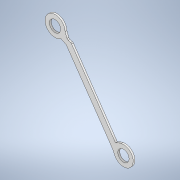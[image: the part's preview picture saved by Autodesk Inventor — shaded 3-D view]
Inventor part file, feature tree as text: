
AUTODESK INVENTOR PART (.ipt)
format: ipt  version: 2022 (Build 260153000, 153)  size: 147,968 bytes
history: native  units: in
note: dims shown in document units (in); Inventor stores cm internally (conversion verified against a paired STEP export)
features: other x1, extrude x1, sketch x1
ambient origin geometry x8: Origin, YZ Plane, XZ Plane, XY Plane, X Axis, Y Axis, Z Axis, Center Point
bodies: Body1 (feature_tree)
feature tree (3):
  other  "Sólido1"
  extrude  "Extrusión1"  Depth=0.0787in
  sketch  "Boceto1"  dims[d7=0.0984in d8=0.1766in d9=0.0984in d10=0.1701in d11=0.6024in d12=0.687in d14=0.0157in d15=0.0157in d16=0.0in d17=0.0787in]
